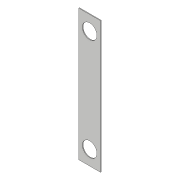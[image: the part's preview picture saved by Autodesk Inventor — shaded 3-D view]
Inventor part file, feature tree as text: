
AUTODESK INVENTOR PART (.ipt)
format: ipt  version: 2019 (Build 230136000, 136)  size: 91,136 bytes
history: native  units: mm
features: sketch x2, sheet_metal_op x1, extrude x1, other x1
ambient origin geometry x8: Origin, YZ Plane, XZ Plane, XY Plane, X Axis, Y Axis, Z Axis, Center Point
bodies: Solid1 (feature_tree)
feature tree (5):
  sheet_metal_op  "Face1"
  extrude  "Extrusion1"  Depth=90.0mm
  sketch  "Sketch1"  dims[d0=15.0mm d1=90.0mm]
  other  "Plate1"
  sketch  "Sketch2"  dims[d2=0.5mm d3=10.0mm d4=10.0mm d5=10.0mm d6=10.0mm d7=10.0mm d8=0.0mm]
